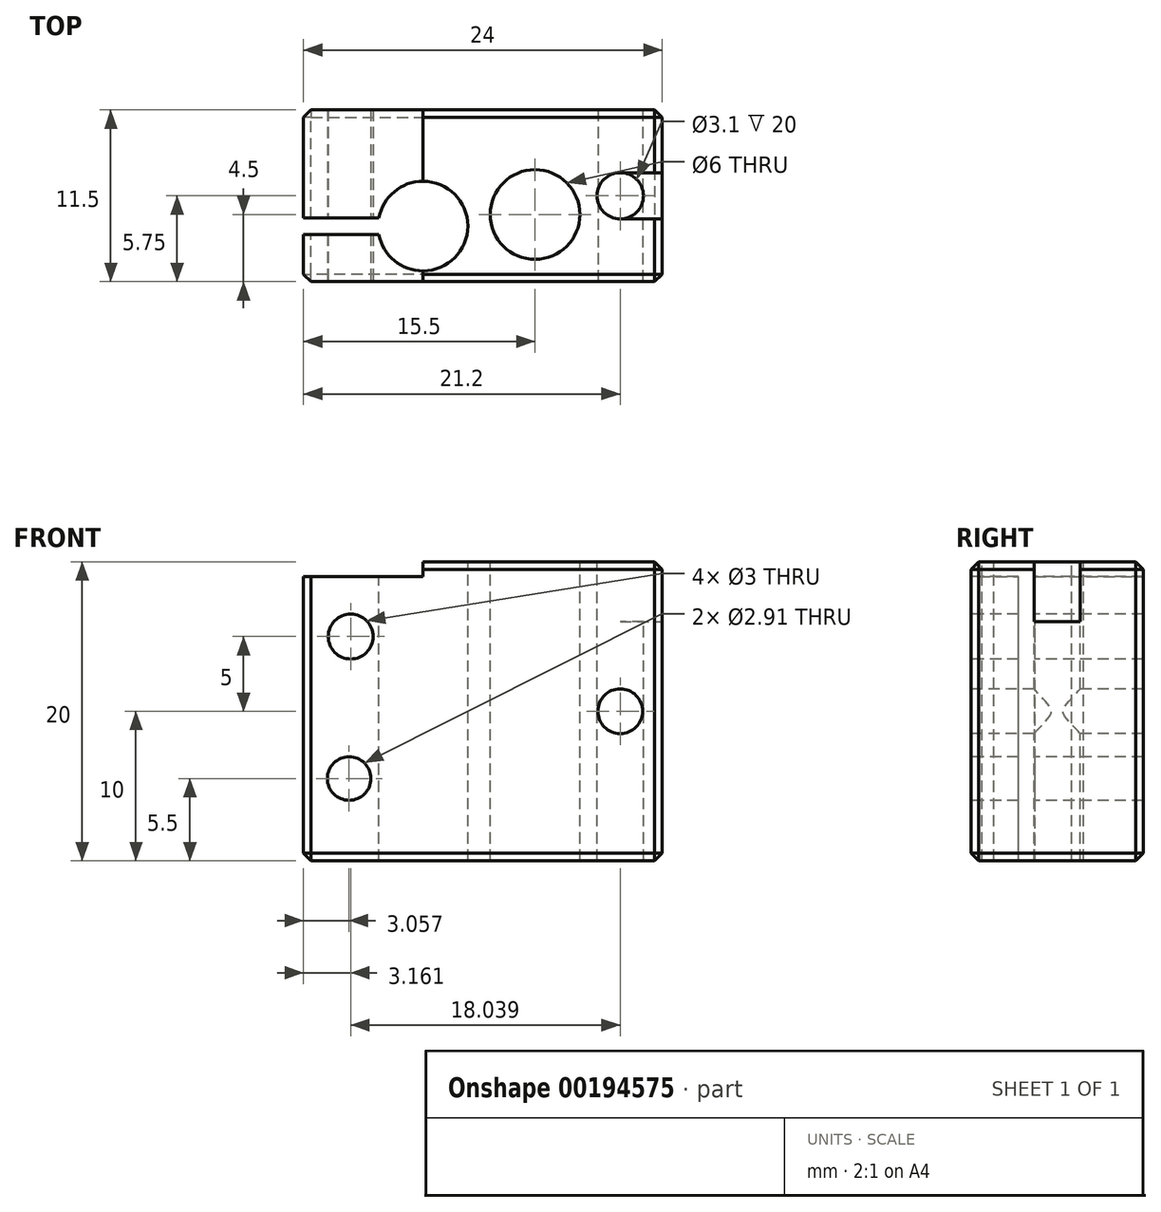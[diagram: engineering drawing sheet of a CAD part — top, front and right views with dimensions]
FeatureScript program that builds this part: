
annotation { "Feature Type Name" : "Feature", "Feature Type Description" : "" }
export const myFeature = defineFeature(function(context is Context, id is Id, definition is map)
    precondition{}
    {
        {
            var Q0;
            Q0=qCreatedBy(makeId("Top.planeOp"),FACE);
            var sketch = newSketch(context, id + "F0", { "sketchPlane" : qUnion([Q0])});
            skLineSegment(sketch, "E0.bottom", {"start": v(0, 0) * mm, "end": v(24, 0) * mm});
            skLineSegment(sketch, "E0.top", {"start": v(0, 11.5) * mm, "end": v(24, 11.5) * mm});
            skLineSegment(sketch, "E0.left", {"start": v(0, 0) * mm, "end": v(0, 11.5) * mm});
            skLineSegment(sketch, "E0.right", {"start": v(24, 0) * mm, "end": v(24, 11.5) * mm});
            skSolve(sketch);
        }
        {
            var Q0;
            Q0 = qSketchRegion(id + "F0", true);
            extrude(context, id + "F1", {"entities" : qUnion([Q0]), "depth" : 20 * mm});
        }
        {
            var Q0;
            Q0=makeQuery(id+"F1.opExtrude","CAP_FACE",FACE,{"disambiguationData":[OSD([sQuery(id+"F0.wireOp",EDGE,"E0.bottom"),sQuery(id+"F0.wireOp",EDGE,"E0.top"),sQuery(id+"F0.wireOp",EDGE,"E0.left"),sQuery(id+"F0.wireOp",EDGE,"E0.right")])],"isStart":false});
            var sketch = newSketch(context, id + "F2", { "sketchPlane" : qUnion([Q0])});
            skCircle(sketch, "E1", {"center": v(21.2, 5.75) * mm, "radius": 1.55 * mm});
            skCircle(sketch, "E2", {"center": v(15.5, 4.5) * mm, "radius": 3 * mm});
            skCircle(sketch, "E3", {"center": v(8, 3.72) * mm, "radius": 3 * mm});
            skSolve(sketch);
        }
        {
            var Q0;
            Q0=makeQuery(id+"F2.imprint","IMPRINT",FACE,{"disambiguationData":[TD([[makeQuery(id+"F2.imprint","IMPRINT",EDGE,{"derivedFrom":sQuery(id+"F2.wireOp",EDGE,"E3")}),1.0]])]});
            var Q1;
            Q1=makeQuery(id+"F2.imprint","IMPRINT",FACE,{"disambiguationData":[TD([[makeQuery(id+"F2.imprint","IMPRINT",EDGE,{"derivedFrom":sQuery(id+"F2.wireOp",EDGE,"E2")}),1.0]])]});
            var Q2;
            Q2=makeQuery(id+"F2.imprint","IMPRINT",FACE,{"disambiguationData":[TD([[makeQuery(id+"F2.imprint","IMPRINT",EDGE,{"derivedFrom":sQuery(id+"F2.wireOp",EDGE,"E1")}),1.0]])]});
            var Q3;
            Q3=sQuery(id+"F2.wireOp",EDGE,"E2");
            var Q4;
            Q4=sQuery(id+"F2.wireOp",EDGE,"E1");
            var Q5;
            Q5=sQuery(id+"F2.wireOp",EDGE,"E3");
            extrude(context, id + "F3", {"entities" : qUnion([Q0, Q1, Q2]), "operationType" : NewBodyOperationType.REMOVE, "surfaceEntities" : qUnion([Q3, Q4, Q5]), "endBound" : BoundingType.THROUGH_ALL, "oppositeDirection" : true, "depth" : 25 * mm});
        }
        {
            var Q0;
            Q0=makeQuery(id+"F1.opExtrude","SWEPT_FACE",FACE,{"disambiguationData":[OSD([sQuery(id+"F0.wireOp",EDGE,"E0.bottom")])]});
            var sketch = newSketch(context, id + "F4", { "sketchPlane" : qUnion([Q0])});
            skCircle(sketch, "E4", {"center": v(21.2, 10) * mm, "radius": 1.5 * mm});
            skCircle(sketch, "E5", {"center": v(3.06, 5.5) * mm, "radius": 1.46 * mm});
            skCircle(sketch, "E6", {"center": v(3.16, 15) * mm, "radius": 1.5 * mm});
            skSolve(sketch);
        }
        {
            var Q0;
            Q0 = qSketchRegion(id + "F4", true);
            extrude(context, id + "F5", {"entities" : qUnion([Q0]), "operationType" : NewBodyOperationType.REMOVE, "endBound" : BoundingType.THROUGH_ALL, "oppositeDirection" : true, "depth" : 25 * mm});
        }
        {
            var Q0;
            Q0=makeQuery(id+"F1.opExtrude","CAP_FACE",FACE,{"disambiguationData":[OSD([sQuery(id+"F0.wireOp",EDGE,"E0.bottom"),sQuery(id+"F0.wireOp",EDGE,"E0.top"),sQuery(id+"F0.wireOp",EDGE,"E0.left"),sQuery(id+"F0.wireOp",EDGE,"E0.right")])],"isStart":false});
            var sketch = newSketch(context, id + "F6", { "sketchPlane" : qUnion([Q0])});
            skLineSegment(sketch, "E7", {"start": v(21.2, 7.3) * mm, "end": v(24, 7.3) * mm});
            skLineSegment(sketch, "E8", {"start": v(21.2, 4.2) * mm, "end": v(24, 4.2) * mm});
            skSolve(sketch);
        }
        {
            var Q0;
            {var subQ0=sQuery(id+"F6.wireOp",EDGE,"E7");Q0=makeQuery(id+"F6.imprint","IMPRINT",FACE,{"disambiguationData":[TD([[makeQuery(id+"F6.imprint","IMPRINT",EDGE,{"derivedFrom":subQ0}),-1.0]])]});}
            extrude(context, id + "F7", {"entities" : qUnion([Q0]), "operationType" : NewBodyOperationType.REMOVE, "oppositeDirection" : true, "depth" : 4 * mm});
        }
        {
            var Q0;
            Q0=makeQuery(id+"F1.opExtrude","CAP_FACE",FACE,{"disambiguationData":[OSD([sQuery(id+"F0.wireOp",EDGE,"E0.bottom"),sQuery(id+"F0.wireOp",EDGE,"E0.top"),sQuery(id+"F0.wireOp",EDGE,"E0.left"),sQuery(id+"F0.wireOp",EDGE,"E0.right")])],"isStart":false});
            var sketch = newSketch(context, id + "F8", { "sketchPlane" : qUnion([Q0])});
            skLineSegment(sketch, "E9", {"start": v(8, 11.5) * mm, "end": v(8, 0) * mm});
            skSolve(sketch);
        }
        {
            var Q0;
            {var subQ0=makeQuery(id+"F1.opExtrude","CAP_EDGE",EDGE,{"disambiguationData":[OSD([sQuery(id+"F0.wireOp",EDGE,"E0.left")])],"isStart":false});Q0=makeQuery(id+"F8.imprint","IMPRINT",FACE,{"disambiguationData":[TD([[makeQuery(id+"F8.imprint","IMPRINT",EDGE,{"derivedFrom":subQ0}),-1.0]])]});}
            extrude(context, id + "F9", {"entities" : qUnion([Q0]), "operationType" : NewBodyOperationType.REMOVE, "oppositeDirection" : true, "depth" : 1 * mm});
        }
        {
            var Q0;
            Q0=makeQuery(id+"F9.boolean.opBoolean","COPY",EDGE,{"derivedFrom":makeQuery(id+"F9.opExtrude","CAP_EDGE",EDGE,{"disambiguationData":[OSD([sQuery(id+"F0.wireOp",EDGE,"E0.bottom")])],"isStart":false})});
            var Q1;
            Q1=makeQuery(id+"F9.boolean.opBoolean","COPY",EDGE,{"derivedFrom":makeQuery(id+"F9.opExtrude","CAP_EDGE",EDGE,{"disambiguationData":[OSD([sQuery(id+"F0.wireOp",EDGE,"E0.left")])],"isStart":false})});
            var Q2;
            Q2=makeQuery(id+"F1.opExtrude","SWEPT_EDGE",EDGE,{"disambiguationData":[OSD([sQuery(id+"F0.wireOp",EDGE,"E0.bottom"),sQuery(id+"F0.wireOp",EDGE,"E0.left")])]});
            var Q3;
            Q3=makeQuery(id+"F1.opExtrude","SWEPT_EDGE",EDGE,{"disambiguationData":[OSD([sQuery(id+"F0.wireOp",EDGE,"E0.top"),sQuery(id+"F0.wireOp",EDGE,"E0.left")])]});
            var Q4;
            {var subQ0=sQuery(id+"F8.wireOp",EDGE,"E9");Q4=makeQuery(id+"F9.boolean.opBoolean","COPY",EDGE,{"derivedFrom":makeQuery(id+"F9.opExtrude","CAP_EDGE",EDGE,{"disambiguationData":[OSD([subQ0]),TDD([makeQuery(id+"F8.imprint","IMPRINT",EDGE,{"disambiguationData":[TD([[makeQuery(id+"F8.imprint","INTERSECT",VERTEX,{"derivedFrom":[makeQuery(id+"F1.opExtrude","CAP_EDGE",EDGE,{"disambiguationData":[OSD([sQuery(id+"F0.wireOp",EDGE,"E0.top")])],"isStart":false}),subQ0]}),-1.0]])],"derivedFrom":subQ0})])],"isStart":true})});}
            var Q5;
            {var subQ0=sQuery(id+"F8.wireOp",EDGE,"E9");Q5=makeQuery(id+"F9.boolean.opBoolean","COPY",EDGE,{"derivedFrom":makeQuery(id+"F9.opExtrude","CAP_EDGE",EDGE,{"disambiguationData":[OSD([subQ0]),TDD([makeQuery(id+"F8.imprint","IMPRINT",EDGE,{"disambiguationData":[TD([[makeQuery(id+"F8.imprint","INTERSECT",VERTEX,{"derivedFrom":[makeQuery(id+"F1.opExtrude","CAP_EDGE",EDGE,{"disambiguationData":[OSD([sQuery(id+"F0.wireOp",EDGE,"E0.bottom")])],"isStart":false}),subQ0]}),1.0]])],"derivedFrom":subQ0})])],"isStart":true})});}
            var Q6;
            Q6=makeQuery(id+"F9.boolean.opBoolean","COPY",EDGE,{"derivedFrom":makeQuery(id+"F9.opExtrude","SWEPT_EDGE",EDGE,{"disambiguationData":[OSD([sQuery(id+"F0.wireOp",EDGE,"E0.bottom"),sQuery(id+"F8.wireOp",EDGE,"E9")])]})});
            var Q7;
            Q7=makeQuery(id+"F1.opExtrude","CAP_EDGE",EDGE,{"disambiguationData":[OSD([sQuery(id+"F0.wireOp",EDGE,"E0.bottom")])],"isStart":false});
            var Q8;
            {var subQ0=sQuery(id+"F0.wireOp",EDGE,"E0.bottom");var subQ1=sQuery(id+"F0.wireOp",EDGE,"E0.right");Q8=makeQuery(id+"F7.boolean.opBoolean","SPLIT",EDGE,{"disambiguationData":[TD([makeQuery(id+"F1.opExtrude","SWEPT_FACE",FACE,{"disambiguationData":[OSD([subQ0])]})])],"derivedFrom":makeQuery(id+"F1.opExtrude","CAP_EDGE",EDGE,{"disambiguationData":[OSD([subQ1])],"isStart":false})});}
            var Q9;
            Q9=makeQuery(id+"F7.boolean.opBoolean","COPY",EDGE,{"derivedFrom":makeQuery(id+"F7.opExtrude","CAP_EDGE",EDGE,{"disambiguationData":[OSD([sQuery(id+"F6.wireOp",EDGE,"E8")])],"isStart":true})});
            var Q10;
            {var subQ0=sQuery(id+"F0.wireOp",EDGE,"E0.right");var subQ1=sQuery(id+"F0.wireOp",EDGE,"E0.top");Q10=makeQuery(id+"F7.boolean.opBoolean","SPLIT",EDGE,{"disambiguationData":[TD([makeQuery(id+"F1.opExtrude","SWEPT_FACE",FACE,{"disambiguationData":[OSD([subQ1])]})])],"derivedFrom":makeQuery(id+"F1.opExtrude","CAP_EDGE",EDGE,{"disambiguationData":[OSD([subQ0])],"isStart":false})});}
            var Q11;
            Q11=makeQuery(id+"F1.opExtrude","CAP_EDGE",EDGE,{"disambiguationData":[OSD([sQuery(id+"F0.wireOp",EDGE,"E0.top")])],"isStart":false});
            var Q12;
            Q12=makeQuery(id+"F1.opExtrude","SWEPT_EDGE",EDGE,{"disambiguationData":[OSD([sQuery(id+"F0.wireOp",EDGE,"E0.bottom"),sQuery(id+"F0.wireOp",EDGE,"E0.right")])]});
            var Q13;
            Q13=makeQuery(id+"F1.opExtrude","CAP_EDGE",EDGE,{"disambiguationData":[OSD([sQuery(id+"F0.wireOp",EDGE,"E0.left")])],"isStart":true});
            var Q14;
            Q14=makeQuery(id+"F1.opExtrude","CAP_EDGE",EDGE,{"disambiguationData":[OSD([sQuery(id+"F0.wireOp",EDGE,"E0.bottom")])],"isStart":true});
            var Q15;
            Q15=makeQuery(id+"F1.opExtrude","CAP_EDGE",EDGE,{"disambiguationData":[OSD([sQuery(id+"F0.wireOp",EDGE,"E0.right")])],"isStart":true});
            var Q16;
            Q16=makeQuery(id+"F1.opExtrude","CAP_EDGE",EDGE,{"disambiguationData":[OSD([sQuery(id+"F0.wireOp",EDGE,"E0.top")])],"isStart":true});
            var Q17;
            Q17=makeQuery(id+"F1.opExtrude","SWEPT_EDGE",EDGE,{"disambiguationData":[OSD([sQuery(id+"F0.wireOp",EDGE,"E0.top"),sQuery(id+"F0.wireOp",EDGE,"E0.right")])]});
            var Q18;
            Q18=makeQuery(id+"F9.boolean.opBoolean","COPY",EDGE,{"derivedFrom":makeQuery(id+"F9.opExtrude","CAP_EDGE",EDGE,{"disambiguationData":[OSD([sQuery(id+"F0.wireOp",EDGE,"E0.top")])],"isStart":false})});
            var Q19;
            Q19=makeQuery(id+"F9.boolean.opBoolean","COPY",EDGE,{"derivedFrom":makeQuery(id+"F9.opExtrude","SWEPT_EDGE",EDGE,{"disambiguationData":[OSD([sQuery(id+"F0.wireOp",EDGE,"E0.top"),sQuery(id+"F8.wireOp",EDGE,"E9")])]})});
            var Q20;
            Q20=makeQuery(id+"F3.boolean.opBoolean","COPY",EDGE,{"derivedFrom":makeQuery(id+"F3.opExtrude","CAP_EDGE",EDGE,{"disambiguationData":[OSD([sQuery(id+"F2.wireOp",EDGE,"E2")])],"isStart":true})});
            chamfer(context, id + "F10", {"entities" : qUnion([Q0, Q1, Q2, Q3, Q4, Q5, Q6, Q7, Q8, Q9, Q10, Q11, Q12, Q13, Q14, Q15, Q16, Q17, Q18, Q19, Q20]), "width" : 0.5 * mm, "tangentPropagation" : true});
        }
        {
            var Q0;
            Q0=makeQuery(id+"F9.boolean.opBoolean","COPY",FACE,{"derivedFrom":makeQuery(id+"F9.opExtrude","CAP_FACE",FACE,{"disambiguationData":[OSD([sQuery(id+"F0.wireOp",EDGE,"E0.bottom"),sQuery(id+"F0.wireOp",EDGE,"E0.top"),sQuery(id+"F0.wireOp",EDGE,"E0.left"),sQuery(id+"F2.wireOp",EDGE,"E3"),sQuery(id+"F8.wireOp",EDGE,"E9")])],"isStart":false})});
            var sketch = newSketch(context, id + "F11", { "sketchPlane" : qUnion([Q0])});
            skLineSegment(sketch, "E10", {"start": v(10.63, 4.26) * mm, "end": v(-3.7, 4.26) * mm});
            skLineSegment(sketch, "E11", {"start": v(-3.7, 4.26) * mm, "end": v(-3.7, 3.16) * mm});
            skLineSegment(sketch, "E12", {"start": v(-3.7, 3.16) * mm, "end": v(10.63, 3.16) * mm});
            skLineSegment(sketch, "E13", {"start": v(10.63, 3.16) * mm, "end": v(10.63, 4.26) * mm});
            skSolve(sketch);
        }
        {
            var Q0;
            Q0 = qSketchRegion(id + "F11", true);
            extrude(context, id + "F12", {"entities" : qUnion([Q0]), "operationType" : NewBodyOperationType.REMOVE, "endBound" : BoundingType.THROUGH_ALL, "oppositeDirection" : true, "depth" : 25 * mm});
        }
    });
